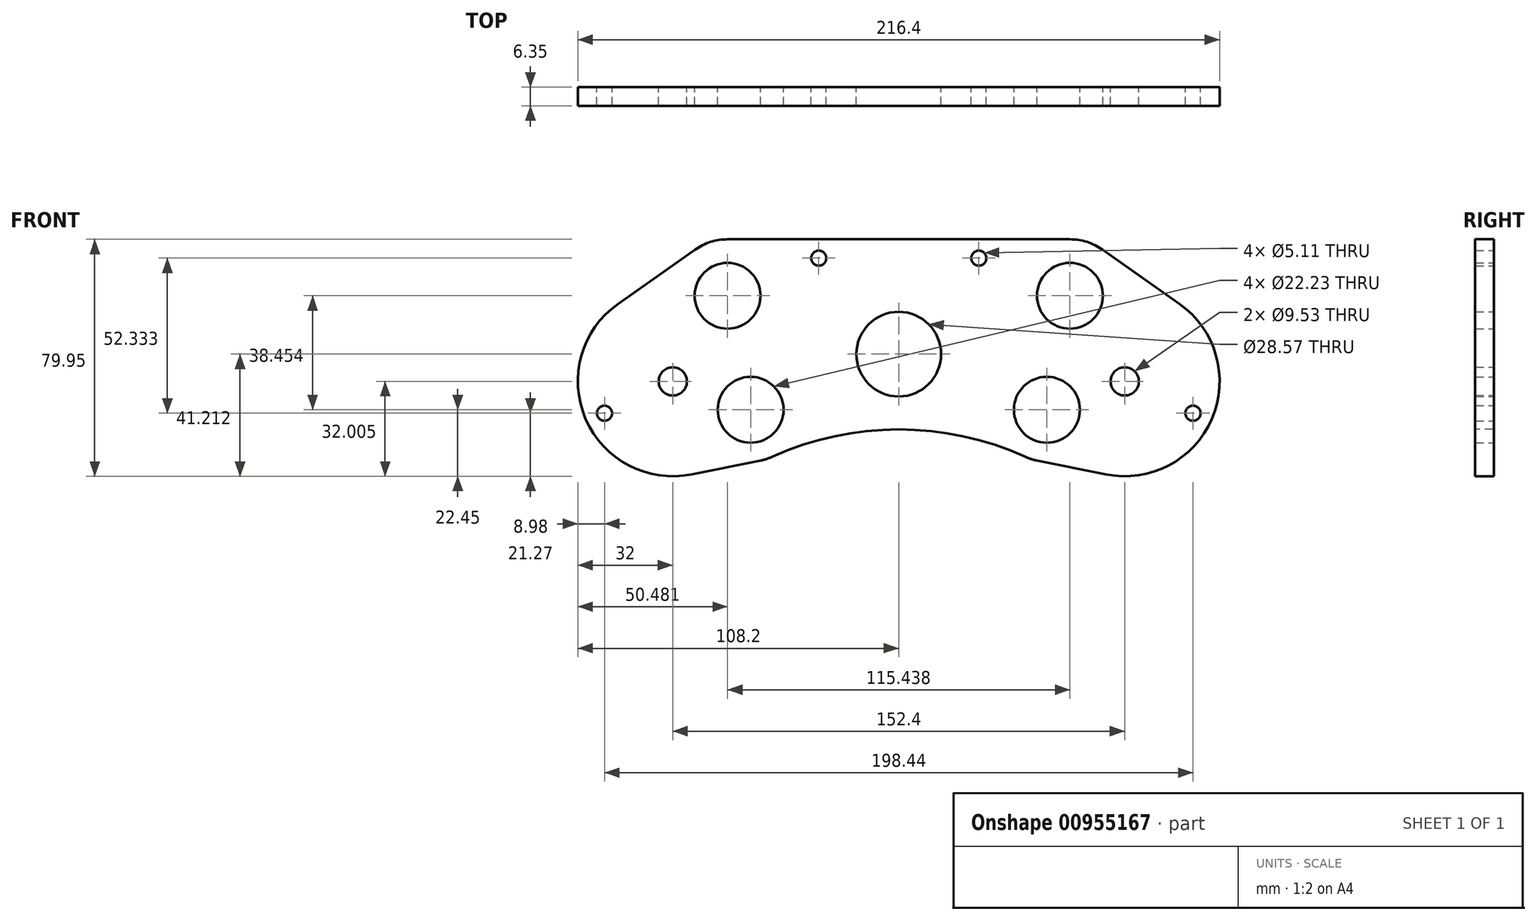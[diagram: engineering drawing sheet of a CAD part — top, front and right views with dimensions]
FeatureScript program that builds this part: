
annotation { "Feature Type Name" : "Feature", "Feature Type Description" : "" }
export const myFeature = defineFeature(function(context is Context, id is Id, definition is map)
    precondition{}
    {
        {
            var Q0;
            Q0=qCreatedBy(makeId("Front.planeOp"),FACE);
            var sketch = newSketch(context, id + "F0", { "sketchPlane" : qUnion([Q0])});
            skCircle(sketch, "E0", {"center": v(-76.2, 60.33) * mm, "radius": 32 * mm, "construction": true});
            skCircle(sketch, "E1", {"center": v(76.2, 60.33) * mm, "radius": 32 * mm, "construction": true});
            skLineSegment(sketch, "E2", {"start": v(-76.2, 60.33) * mm, "end": v(76.2, 60.32) * mm, "construction": true});
            skLineSegment(sketch, "E3", {"start": v(0, 60.33) * mm, "end": v(0, 0) * mm, "construction": true});
            skLineSegment(sketch, "E4.bottom", {"start": v(-101.6, -25.4) * mm, "end": v(101.6, -25.4) * mm, "construction": true});
            skLineSegment(sketch, "E4.top", {"start": v(-101.6, 25.4) * mm, "end": v(101.6, 25.4) * mm, "construction": true});
            skLineSegment(sketch, "E4.left", {"start": v(-101.6, -25.4) * mm, "end": v(-101.6, 25.4) * mm, "construction": true});
            skLineSegment(sketch, "E4.right", {"start": v(101.6, -25.4) * mm, "end": v(101.6, 25.4) * mm, "construction": true});
            skPoint(sketch, "E4.middle", {"position": v(0, 0) * mm});
            skCircle(sketch, "E5", {"center": v(0, -1.59) * mm, "radius": 50.8 * mm, "construction": true});
            skCircle(sketch, "E6", {"center": v(-76.2, 60.33) * mm, "radius": 7.62 * mm, "construction": true});
            skCircle(sketch, "E7", {"center": v(76.2, 60.33) * mm, "radius": 7.62 * mm, "construction": true});
            skCircle(sketch, "E8", {"center": v(0, 69.53) * mm, "radius": 34.3 * mm, "construction": true});
            skCircle(sketch, "E9", {"center": v(0, 69.53) * mm, "radius": 38.1 * mm, "construction": true});
            skCircle(sketch, "E10", {"center": v(0, -1.59) * mm, "radius": 33.02 * mm, "construction": true});
            skCircle(sketch, "E11", {"center": v(0, 69.53) * mm, "radius": 25.4 * mm, "construction": true});
            skCircle(sketch, "E12", {"center": v(0, -1.59) * mm, "radius": 45.72 * mm, "construction": true});
            skCircle(sketch, "E13", {"center": v(-76.2, 60.33) * mm, "radius": 8.9 * mm, "construction": true});
            skCircle(sketch, "E14", {"center": v(76.2, 60.33) * mm, "radius": 8.9 * mm, "construction": true});
            skCircle(sketch, "E15", {"center": v(0, 69.53) * mm, "radius": 14.29 * mm});
            skCircle(sketch, "E16", {"center": v(0, -1.59) * mm, "radius": 14.29 * mm, "construction": true});
            skCircle(sketch, "E17", {"center": v(-88.9, 12.7) * mm, "radius": 2.55 * mm, "construction": true});
            skCircle(sketch, "E18.0.1.0", {"center": v(-88.9, -12.7) * mm, "radius": 2.55 * mm, "construction": true});
            skCircle(sketch, "E18.1.0.0", {"center": v(-63.5, 12.7) * mm, "radius": 2.55 * mm, "construction": true});
            skCircle(sketch, "E18.1.1.0", {"center": v(-63.5, -12.7) * mm, "radius": 2.55 * mm, "construction": true});
            skCircle(sketch, "E18.2.0.0", {"center": v(-38.1, 12.7) * mm, "radius": 2.55 * mm});
            skCircle(sketch, "E18.2.1.0", {"center": v(-38.1, -12.7) * mm, "radius": 2.55 * mm});
            skCircle(sketch, "E18.3.0.0", {"center": v(-12.7, 12.7) * mm, "radius": 2.55 * mm, "construction": true});
            skCircle(sketch, "E18.3.1.0", {"center": v(-12.7, -12.7) * mm, "radius": 2.55 * mm, "construction": true});
            skCircle(sketch, "E18.4.0.0", {"center": v(12.7, 12.7) * mm, "radius": 2.55 * mm, "construction": true});
            skCircle(sketch, "E18.4.1.0", {"center": v(12.7, -12.7) * mm, "radius": 2.55 * mm, "construction": true});
            skCircle(sketch, "E18.5.0.0", {"center": v(38.1, 12.7) * mm, "radius": 2.55 * mm});
            skCircle(sketch, "E18.5.1.0", {"center": v(38.1, -12.7) * mm, "radius": 2.55 * mm});
            skCircle(sketch, "E18.6.0.0", {"center": v(63.5, 12.7) * mm, "radius": 2.55 * mm, "construction": true});
            skCircle(sketch, "E18.6.1.0", {"center": v(63.5, -12.7) * mm, "radius": 2.55 * mm, "construction": true});
            skCircle(sketch, "E18.7.0.0", {"center": v(88.9, 12.7) * mm, "radius": 2.55 * mm, "construction": true});
            skCircle(sketch, "E18.7.1.0", {"center": v(88.9, -12.7) * mm, "radius": 2.55 * mm, "construction": true});
            skLineSegment(sketch, "E18.direction1", {"start": v(-88.9, 12.7) * mm, "end": v(-63.5, 12.7) * mm, "construction": true});
            skLineSegment(sketch, "E18.direction2", {"start": v(-88.9, 12.7) * mm, "end": v(-88.9, -12.7) * mm, "construction": true});
            skArc(sketch, "E19", {"start": v(-99.01, 37.88) * mm, "mid": v(-108.08, 63.18) * mm, "end": v(-94.65, 86.47) * mm});
            skCircle(sketch, "E20", {"center": v(-76.2, 60.33) * mm, "radius": 4.76 * mm});
            skCircle(sketch, "E21", {"center": v(76.2, 60.33) * mm, "radius": 4.76 * mm});
            skLineSegment(sketch, "E22", {"start": v(-99.22, 49.6) * mm, "end": v(-76.2, 60.33) * mm, "construction": true});
            skLineSegment(sketch, "E23", {"start": v(-76.2, 60.33) * mm, "end": v(-53.18, 71.06) * mm, "construction": true});
            skCircle(sketch, "E24", {"center": v(-53.18, 71.06) * mm, "radius": 2.55 * mm, "construction": true});
            skCircle(sketch, "E25", {"center": v(-99.22, 49.6) * mm, "radius": 2.55 * mm});
            skCircle(sketch, "E26.MirrorC", {"center": v(53.18, 71.06) * mm, "radius": 2.55 * mm, "construction": true});
            skLineSegment(sketch, "E27.MirrorCS", {"start": v(76.2, 60.33) * mm, "end": v(53.18, 71.06) * mm, "construction": true});
            skLineSegment(sketch, "E28.MirrorCS", {"start": v(99.22, 49.6) * mm, "end": v(76.2, 60.33) * mm, "construction": true});
            skCircle(sketch, "E29.MirrorC", {"center": v(99.22, 49.6) * mm, "radius": 2.55 * mm});
            skCircle(sketch, "E30", {"center": v(0, -1.59) * mm, "radius": 23.81 * mm, "construction": true});
            skArc(sketch, "E31", {"start": v(3.03, -25.2) * mm, "mid": v(0, -25.4) * mm, "end": v(-3.03, -25.2) * mm});
            skCircle(sketch, "E32", {"center": v(-38.1, -12.7) * mm, "radius": 7.94 * mm, "construction": true});
            skCircle(sketch, "E33", {"center": v(38.1, -12.7) * mm, "radius": 7.94 * mm, "construction": true});
            skLineSegment(sketch, "E34", {"start": v(-3.03, -25.2) * mm, "end": v(-39.11, -20.57) * mm});
            skArc(sketch, "E35", {"start": v(-39.11, -20.57) * mm, "mid": v(-41.63, -19.81) * mm, "end": v(-43.76, -18.27) * mm});
            skLineSegment(sketch, "E36", {"start": v(-43.76, -18.27) * mm, "end": v(-99.01, 37.88) * mm});
            skLineSegment(sketch, "E37", {"start": v(3.03, -25.2) * mm, "end": v(39.11, -20.57) * mm});
            skArc(sketch, "E38", {"start": v(39.11, -20.57) * mm, "mid": v(41.63, -19.81) * mm, "end": v(43.76, -18.27) * mm});
            skLineSegment(sketch, "E39", {"start": v(43.76, -18.27) * mm, "end": v(99.01, 37.88) * mm});
            skCircle(sketch, "E40", {"center": v(-57.72, 89.22) * mm, "radius": 26.68 * mm, "construction": true});
            skCircle(sketch, "E41", {"center": v(-49.94, 50.77) * mm, "radius": 19.05 * mm, "construction": true});
            skCircle(sketch, "E42", {"center": v(57.72, 89.22) * mm, "radius": 26.68 * mm, "construction": true});
            skCircle(sketch, "E43", {"center": v(49.94, 50.77) * mm, "radius": 19.05 * mm, "construction": true});
            skCircle(sketch, "E44", {"center": v(-57.72, 89.22) * mm, "radius": 11.11 * mm});
            skCircle(sketch, "E45", {"center": v(-49.94, 50.77) * mm, "radius": 11.11 * mm});
            skCircle(sketch, "E46", {"center": v(49.94, 50.77) * mm, "radius": 11.11 * mm});
            skCircle(sketch, "E47", {"center": v(57.72, 89.22) * mm, "radius": 11.11 * mm});
            skCircle(sketch, "E48", {"center": v(57.72, 89.22) * mm, "radius": 19.05 * mm, "construction": true});
            skCircle(sketch, "E49", {"center": v(-57.72, 89.22) * mm, "radius": 19.05 * mm, "construction": true});
            skLineSegment(sketch, "E50", {"start": v(-57.72, 108.27) * mm, "end": v(57.72, 108.27) * mm});
            skArc(sketch, "E51", {"start": v(-57.72, 108.27) * mm, "mid": v(-63.48, 107.38) * mm, "end": v(-68.7, 104.79) * mm});
            skLineSegment(sketch, "E52", {"start": v(-68.7, 104.79) * mm, "end": v(-94.65, 86.47) * mm});
            skArc(sketch, "E53", {"start": v(57.72, 108.27) * mm, "mid": v(63.48, 107.38) * mm, "end": v(68.7, 104.79) * mm});
            skArc(sketch, "E54", {"start": v(99.01, 37.88) * mm, "mid": v(108.08, 63.18) * mm, "end": v(94.65, 86.47) * mm});
            skLineSegment(sketch, "E55", {"start": v(94.65, 86.47) * mm, "end": v(68.7, 104.79) * mm});
            skCircle(sketch, "E56", {"center": v(-49.94, 50.77) * mm, "radius": 17.46 * mm, "construction": true});
            skCircle(sketch, "E57", {"center": v(49.94, 50.77) * mm, "radius": 17.46 * mm, "construction": true});
            skLineSegment(sketch, "E58", {"start": v(-26.99, 101.92) * mm, "end": v(26.99, 101.92) * mm, "construction": true});
            skLineSegment(sketch, "E59", {"start": v(0, 101.92) * mm, "end": v(0, 69.53) * mm, "construction": true});
            skCircle(sketch, "E60", {"center": v(-26.99, 101.92) * mm, "radius": 2.55 * mm});
            skCircle(sketch, "E61", {"center": v(26.99, 101.92) * mm, "radius": 2.55 * mm});
            skCircle(sketch, "E62", {"center": v(26.99, 101.92) * mm, "radius": 6.35 * mm, "construction": true});
            skCircle(sketch, "E63", {"center": v(-26.99, 101.92) * mm, "radius": 6.35 * mm, "construction": true});
            skSolve(sketch);
        }
        {
            var Q0;
            Q0=qSketchRegion(id+"F0",true);
            extrude(context, id + "F1", {"entities" : qUnion([Q0]), "depth" : 6.35 * mm, "offsetDistance" : 25.4 * mm});
        }
        {
            var Q0;
            Q0=makeQuery(id+"F1.opExtrude","CAP_FACE",FACE,{"disambiguationData":[OSD([sQuery(id+"F0.wireOp",EDGE,"E15"),sQuery(id+"F0.wireOp",EDGE,"E18.2.0.0"),sQuery(id+"F0.wireOp",EDGE,"E18.2.1.0"),sQuery(id+"F0.wireOp",EDGE,"E18.5.0.0"),sQuery(id+"F0.wireOp",EDGE,"E18.5.1.0"),sQuery(id+"F0.wireOp",EDGE,"E19"),sQuery(id+"F0.wireOp",EDGE,"E20"),sQuery(id+"F0.wireOp",EDGE,"E21"),sQuery(id+"F0.wireOp",EDGE,"E31"),sQuery(id+"F0.wireOp",EDGE,"E34"),sQuery(id+"F0.wireOp",EDGE,"E35"),sQuery(id+"F0.wireOp",EDGE,"E36"),sQuery(id+"F0.wireOp",EDGE,"E37"),sQuery(id+"F0.wireOp",EDGE,"E38"),sQuery(id+"F0.wireOp",EDGE,"E39"),sQuery(id+"F0.wireOp",EDGE,"E44"),sQuery(id+"F0.wireOp",EDGE,"E45"),sQuery(id+"F0.wireOp",EDGE,"E46"),sQuery(id+"F0.wireOp",EDGE,"E47"),sQuery(id+"F0.wireOp",EDGE,"E50"),sQuery(id+"F0.wireOp",EDGE,"E51"),sQuery(id+"F0.wireOp",EDGE,"E52"),sQuery(id+"F0.wireOp",EDGE,"E53"),sQuery(id+"F0.wireOp",EDGE,"E54"),sQuery(id+"F0.wireOp",EDGE,"E55")])],"isStart":false});
            var sketch = newSketch(context, id + "F2", { "sketchPlane" : qUnion([Q0])});
            skArc(sketch, "E64", {"start": v(-99.01, 37.88) * mm, "mid": v(-85.58, 29.73) * mm, "end": v(-69.9, 28.95) * mm});
            skArc(sketch, "E65", {"start": v(69.9, 28.95) * mm, "mid": v(85.58, 29.73) * mm, "end": v(99.01, 37.88) * mm});
            skLineSegment(sketch, "E66", {"start": v(-99.01, 37.88) * mm, "end": v(-99.01, -25.4) * mm});
            skLineSegment(sketch, "E67", {"start": v(-99.01, -25.4) * mm, "end": v(99.01, -25.4) * mm});
            skLineSegment(sketch, "E68", {"start": v(99.01, -25.4) * mm, "end": v(99.01, 37.88) * mm});
            skArc(sketch, "E69", {"start": v(-46.5, 33.65) * mm, "mid": v(-44.57, 34.15) * mm, "end": v(-42.71, 34.87) * mm});
            skArc(sketch, "E70", {"start": v(42.71, 34.87) * mm, "mid": v(0, 44.13) * mm, "end": v(-42.71, 34.87) * mm});
            skArc(sketch, "E71", {"start": v(42.71, 34.87) * mm, "mid": v(44.57, 34.15) * mm, "end": v(46.5, 33.65) * mm});
            skPoint(sketch, "E72.visualSharp", {"position": v(56.94, 34.77) * mm});
            skPoint(sketch, "E73.visualSharp", {"position": v(-56.94, 34.77) * mm});
            skLineSegment(sketch, "E74", {"start": v(-69.9, 28.95) * mm, "end": v(-46.5, 33.65) * mm});
            skLineSegment(sketch, "E75", {"start": v(46.5, 33.65) * mm, "end": v(69.9, 28.95) * mm});
            skSolve(sketch);
        }
        {
            var Q0;
            Q0=qSketchRegion(id+"F2",true);
            extrude(context, id + "F3", {"entities" : qUnion([Q0]), "operationType" : NewBodyOperationType.REMOVE, "oppositeDirection" : true, "depth" : 25.4 * mm, "offsetDistance" : 25.4 * mm});
        }
    });
